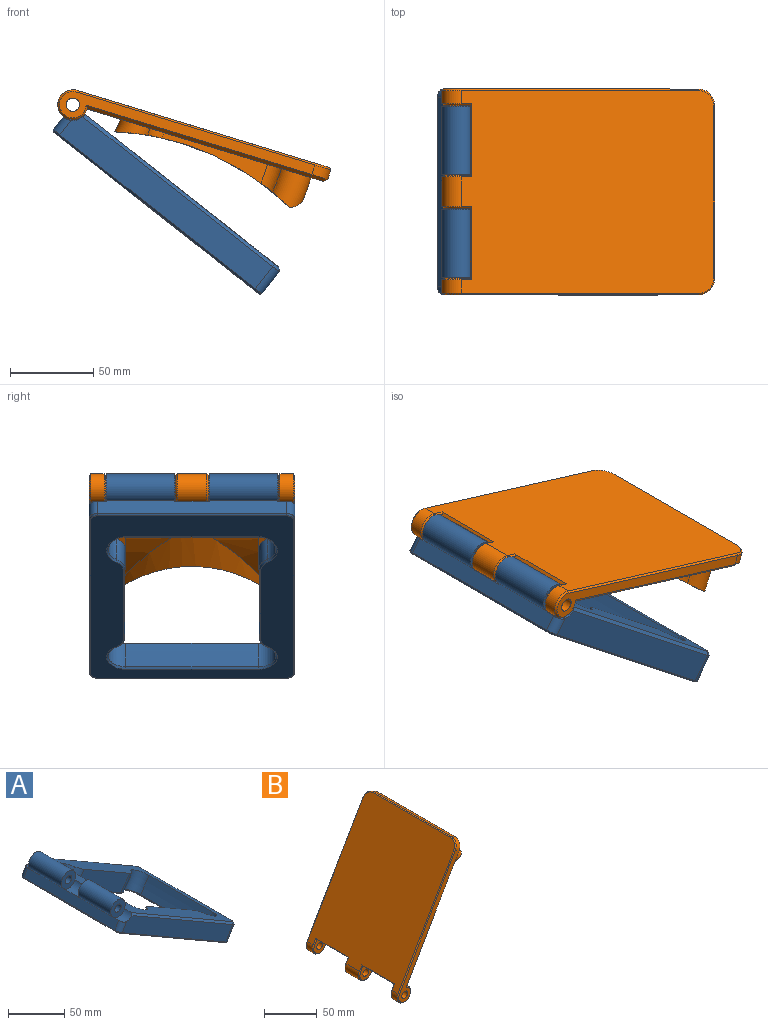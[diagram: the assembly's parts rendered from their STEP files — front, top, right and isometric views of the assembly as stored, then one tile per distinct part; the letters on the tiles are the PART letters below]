
ASSEMBLY  parts=2 mates=1
PART A: 58 faces, bbox 147.2x124.1x105.9 mm
  f0: plane 129.04x120mm, normal (0.5,0,0.87), area 7421.1mm2, adj f1,f3,f4,f6,f8,f9,f14,f15
  f1: plane 18.5x18mm, normal (0,-1,0), area 211.5mm2, adj f0,f2,f4,f5,f28
  f2: cylinder r=4mm len=41mm, axis (0,1,0), area 1030.4mm2, adj f1,f3
  f3: plane 18.5x18mm, normal (0,1,0), area 211.5mm2, adj f0,f2,f4,f5,f27
  f4: cylinder r=9mm len=41mm, axis (0,1,0), area 1738.9mm2, adj f0,f1,f3,f5
  f5: plane 114x8.66mm, normal (-0.87,0,0.5), area 1124mm2, adj f1,f3,f4,f6,f8,f9,f26,f27
  f6: plane 18.5x18mm, normal (0,-1,0), area 211.5mm2, adj f0,f5,f7,f9,f26
  f7: cylinder r=4mm len=41mm, axis (0,1,0), area 1030.4mm2, adj f6,f8
  f8: plane 18.5x18mm, normal (0,1,0), area 211.5mm2, adj f0,f5,f7,f9,f28
  f9: cylinder r=9mm len=41mm, axis (0,1,0), area 1738.9mm2, adj f0,f5,f6,f8
  f10: plane 138.4x87.58mm, normal (0,1,0), area 2533.2mm2, adj f27,f29,f32,f39,f53
  f11: plane 136.92x122.09mm, normal (-0.5,0,-0.87), area 7828.6mm2, adj f33,f34,f35,f36,f37,f38,f39,f40
  f12: plane 114x14.72mm, normal (0.87,0,-0.5), area 1938mm2, adj f29,f30,f35,f55
  f13: plane 138.4x87.58mm, normal (0,-1,0), area 2533.2mm2, adj f26,f30,f31,f34,f57
  f14: torus R=57.32mm, axis (0,1,0), area 192.7mm2, adj f0,f15,f25,f41
  f15: torus R=40mm, axis (0,1,0), area 561.5mm2, adj f0,f14,f16,f43
  f16: cylinder r=29.6mm len=80mm, axis (0,1,0), area 1720.6mm2, adj f0,f15,f17,f45
  f17: torus R=40mm, axis (0,1,0), area 561.5mm2, adj f0,f16,f18,f47
  f18: torus R=57.32mm, axis (0,1,0), area 192.8mm2, adj f0,f17,f19,f49
  f19: plane 68.91x48.4mm, normal (0,1,0), area 1252.8mm2, adj f0,f18,f20,f51
  f20: torus R=122.68mm, axis (0,1,0), area 193.1mm2, adj f0,f19,f21,f52
  f21: torus R=140mm, axis (0,1,0), area 525.4mm2, adj f0,f20,f22,f50
  f22: cylinder r=150.4mm len=80mm, axis (0,1,0), area 1514mm2, adj f0,f21,f23,f48
  f23: torus R=140mm, axis (0,1,0), area 525.4mm2, adj f0,f22,f24,f46
  f24: torus R=122.68mm, axis (0,1,0), area 193.1mm2, adj f0,f23,f25,f44
  f25: plane 68.92x48.4mm, normal (0,-1,0), area 1252.9mm2, adj f0,f14,f24,f42
  f26: cylinder r=9.5mm len=12.98mm, axis (0,1,0), area 149.2mm2, adj f0,f5,f6,f13,f31,f57
  f27: cylinder r=9.5mm len=12.98mm, axis (0,1,0), area 149.2mm2, adj f0,f3,f5,f10,f32,f53
  f28: cylinder r=9.5mm len=21mm, axis (0,1,0), area 313.4mm2, adj f0,f1,f5,f8
  f29: cylinder r=5mm len=17.22mm, axis (0.5,0,0.87), area 133.5mm2, adj f10,f12,f37,f54
  f30: cylinder r=5mm len=17.22mm, axis (-0.5,0,-0.87), area 133.5mm2, adj f12,f13,f33,f56
  f31: cylinder r=5mm len=11.96mm, axis (0.5,0,0.87), area 80.2mm2, adj f5,f13,f26,f36
  f32: cylinder r=5mm len=11.96mm, axis (-0.5,0,-0.87), area 80.2mm2, adj f5,f10,f27,f40
  f33: cone r=4mm half-angle=45deg, axis (0.5,0,0.87), area 10mm2, adj f11,f30,f34,f35
  f34: plane 130.4x75.87mm, normal (-0.35,-0.71,-0.61), area 212.1mm2, adj f11,f13,f33,f36
  f35: plane 114x1.37mm, normal (0.26,0,-0.97), area 161.2mm2, adj f11,f12,f33,f37
  f36: cone r=4mm half-angle=45deg, axis (0.5,0,0.87), area 10mm2, adj f11,f31,f34,f38
  f37: cone r=4mm half-angle=45deg, axis (0.5,0,0.87), area 10mm2, adj f11,f29,f35,f39
  f38: plane 114x1.37mm, normal (-0.97,0,-0.26), area 161.2mm2, adj f5,f11,f36,f40
  f39: plane 130.4x75.87mm, normal (-0.35,0.71,-0.61), area 212.1mm2, adj f10,f11,f37,f40
  f40: cone r=4mm half-angle=45deg, axis (0.5,0,0.87), area 10mm2, adj f11,f32,f38,f39
  f41: bspline ~7.43x5.54mm, area 15.2mm2, adj f11,f14,f42,f43
  f42: plane 58.63x34.43mm, normal (-0.35,-0.71,-0.61), area 94.5mm2, adj f11,f25,f41,f44
  f43: bspline ~21.44x12.38mm, area 39.9mm2, adj f11,f15,f41,f45
  f44: bspline ~7.7x5.33mm, area 13.1mm2, adj f11,f24,f42,f46
  f45: plane 80x0.82mm, normal (-0.1,0,-0.99), area 65.5mm2, adj f11,f16,f43,f47
  f46: bspline ~18.6x11.66mm, area 41mm2, adj f11,f23,f44,f48
  f47: bspline ~21.44x12.38mm, area 39.9mm2, adj f11,f17,f45,f49
  f48: plane 80x1.47mm, normal (-0.98,0,-0.2), area 120mm2, adj f11,f22,f46,f50
  f49: bspline ~7.43x5.54mm, area 15.2mm2, adj f11,f18,f47,f51
  f50: bspline ~18.6x11.65mm, area 41mm2, adj f11,f21,f48,f52
  f51: plane 58.63x34.43mm, normal (-0.35,0.71,-0.61), area 94.8mm2, adj f11,f19,f49,f52
  f52: bspline ~7.7x5.33mm, area 13.1mm2, adj f11,f20,f50,f51
  f53: plane 127.2x74.49mm, normal (0.35,0.71,0.61), area 411.7mm2, adj f0,f10,f27,f54
  f54: cone r=3mm half-angle=45deg, axis (-0.5,0,-0.87), area 17.8mm2, adj f0,f29,f53,f55
  f55: plane 114x2.73mm, normal (0.97,0,0.26), area 322.4mm2, adj f0,f12,f54,f56
  f56: cone r=3mm half-angle=45deg, axis (-0.5,0,-0.87), area 17.8mm2, adj f0,f30,f55,f57
  f57: plane 127.2x74.49mm, normal (0.35,-0.71,0.61), area 411.7mm2, adj f0,f13,f26,f56
PART B: 57 faces, bbox 102.5x124.1x151.6 mm
  f0: cylinder r=4mm len=20mm, axis (0,1,0), area 502.7mm2, adj f8,f9
  f1: cylinder r=4mm len=10mm, axis (0,1,0), area 251.3mm2, adj f11,f12
  f2: plane 129.9x120mm, normal (0.87,0,-0.5), area 7552mm2, adj f4,f6,f8,f9,f10,f11,f13,f18
  f3: plane 137.7x122mm, normal (-0.87,0,0.5), area 18764.8mm2, adj f6,f10,f13,f36,f37,f38,f41,f42
  f4: plane 17.57x16mm, normal (0,-1,0), area 166.7mm2, adj f2,f5,f34,f40,f41,f42
  f5: cylinder r=4mm len=10mm, axis (0,1,0), area 251.3mm2, adj f4,f7
  f6: cylinder r=9mm len=18mm, axis (0,1,0), area 339.8mm2, adj f2,f3,f40,f45,f56
  f7: plane 141.9x81.27mm, normal (0,1,0), area 1016.4mm2, adj f5,f15,f45,f46,f56
  f8: plane 17.57x16mm, normal (0,-1,0), area 166.7mm2, adj f0,f2,f33,f35,f36,f37
  f9: plane 17.57x16mm, normal (0,1,0), area 166.7mm2, adj f0,f2,f34,f42,f43,f44
  f10: cylinder r=9mm len=18mm, axis (0,1,0), area 763.4mm2, adj f2,f3,f35,f44
  f11: plane 17.57x16mm, normal (0,1,0), area 166.7mm2, adj f1,f2,f33,f37,f38,f39
  f12: plane 141.9x81.27mm, normal (0,-1,0), area 1016.4mm2, adj f1,f16,f50,f51,f52
  f13: cylinder r=9mm len=18mm, axis (0,1,0), area 339.8mm2, adj f2,f3,f39,f51,f52
  f14: plane 104x5.2mm, normal (0.5,0,0.87), area 624mm2, adj f15,f16,f48,f54
  f15: cylinder r=10mm len=11.66mm, axis (0.87,0,-0.5), area 94.2mm2, adj f7,f14,f47,f55
  f16: cylinder r=10mm len=11.66mm, axis (0.87,0,-0.5), area 94.2mm2, adj f12,f14,f49,f53
  f17: cylinder r=158.38mm len=92.47mm, axis (0,1,0), area 2497.1mm2, adj f18,f19,f20,f27,f28,f29,f31,f32
  f18: torus R=57.32mm, axis (0,1,0), area 41.4mm2, adj f2,f17,f19,f29
  f19: torus R=40mm, axis (0,1,0), area 169mm2, adj f2,f17,f18,f20
  f20: cylinder r=30mm len=80mm, axis (0,1,0), area 471mm2, adj f2,f17,f19,f21,f30,f31
  f21: torus R=40mm, axis (0,1,0), area 169mm2, adj f2,f20,f22,f30
  f22: torus R=57.32mm, axis (0,1,0), area 41.4mm2, adj f2,f21,f23,f30
  f23: plane 58.43x42.77mm, normal (0,-1,0), area 357mm2, adj f2,f22,f24,f30
  f24: torus R=122.68mm, axis (0,1,0), area 144mm2, adj f2,f23,f25,f30
  f25: torus R=140mm, axis (0,1,0), area 470.2mm2, adj f2,f24,f26,f30,f32
  f26: cylinder r=150mm len=80mm, axis (0,1,0), area 537.6mm2, adj f2,f25,f27,f32
  f27: torus R=140mm, axis (0,1,0), area 470.2mm2, adj f2,f17,f26,f28,f32
  f28: torus R=122.68mm, axis (0,1,0), area 144mm2, adj f2,f17,f27,f29
  f29: plane 58.43x42.77mm, normal (0,1,0), area 357mm2, adj f2,f17,f18,f28
  f30: cylinder r=158.38mm len=92.47mm, axis (0,1,0), area 2497.1mm2, adj f20,f21,f22,f23,f24,f25,f31,f32
  f31: cylinder r=75.17mm len=55.47mm, axis (0.5,0,0.87), area 1104mm2, adj f17,f20,f30
  f32: cylinder r=75.17mm len=97.83mm, axis (0.5,0,0.87), area 4486.4mm2, adj f17,f25,f26,f27,f30
  f33: cylinder r=9.5mm len=42mm, axis (0,1,0), area 345.6mm2, adj f2,f8,f11,f37
  f34: cylinder r=9.5mm len=42mm, axis (0,1,0), area 345.6mm2, adj f2,f4,f9,f42
  f35: cone r=9mm half-angle=45deg, axis (0,1,0), area 56.6mm2, adj f2,f8,f10,f36
  f36: plane 6.39x4.08mm, normal (-0.61,-0.71,0.35), area 9.4mm2, adj f3,f8,f35,f37
  f37: plane 44x1.44mm, normal (-0.77,0,-0.64), area 79.9mm2, adj f3,f8,f11,f33,f36,f38
  f38: plane 6.39x4.08mm, normal (-0.61,0.71,0.35), area 9.4mm2, adj f3,f11,f37,f39
  f39: cone r=8mm half-angle=45deg, axis (0,-1,0), area 56.6mm2, adj f2,f11,f13,f38
  f40: cone r=9mm half-angle=45deg, axis (0,1,0), area 56.6mm2, adj f2,f4,f6,f41
  f41: plane 6.39x4.08mm, normal (-0.61,-0.71,0.35), area 9.4mm2, adj f3,f4,f40,f42
  f42: plane 44x1.44mm, normal (-0.77,0,-0.64), area 79.9mm2, adj f3,f4,f9,f34,f41,f43
  f43: plane 6.39x4.08mm, normal (-0.61,0.71,0.35), area 9.4mm2, adj f3,f9,f42,f44
  f44: cone r=8mm half-angle=45deg, axis (0,-1,0), area 56.6mm2, adj f2,f9,f10,f43
  f45: cone r=8mm half-angle=45deg, axis (0,-1,0), area 58.8mm2, adj f6,f7,f46,f56
  f46: plane 130.4x75.87mm, normal (-0.61,0.71,0.35), area 212.1mm2, adj f3,f7,f45,f47
  f47: cone r=9mm half-angle=45deg, axis (0.87,0,-0.5), area 21.1mm2, adj f3,f15,f46,f48
  f48: plane 104x1.37mm, normal (-0.26,0,0.97), area 147.1mm2, adj f3,f14,f47,f49
  f49: cone r=9mm half-angle=45deg, axis (0.87,0,-0.5), area 21.1mm2, adj f3,f16,f48,f50
  f50: plane 130.4x75.87mm, normal (-0.61,-0.71,0.35), area 212.1mm2, adj f3,f12,f49,f51
  f51: cone r=9mm half-angle=45deg, axis (0,1,0), area 58.8mm2, adj f12,f13,f50,f52
  f52: plane 123.26x72.92mm, normal (0.61,-0.71,-0.35), area 399.7mm2, adj f2,f12,f13,f51,f53
  f53: cone r=10mm half-angle=45deg, axis (-0.87,0,0.5), area 40mm2, adj f2,f16,f52,f54
  f54: plane 104x2.73mm, normal (0.97,0,0.26), area 294.2mm2, adj f2,f14,f53,f55
  f55: cone r=10mm half-angle=45deg, axis (-0.87,0,0.5), area 40mm2, adj f2,f15,f54,f56
  f56: plane 123.26x72.92mm, normal (0.61,0.71,-0.35), area 399.7mm2, adj f2,f6,f7,f45,f55
PLACE A rot(axis=(0,1,0),8.2deg) t=(-67.58,27.36,170.81)mm
PLACE B rot(axis=(0,1,0),77deg) t=(-136.42,27.36,96.02)mm
MATE revolute B.f19 <-> A.f2  axis (0,-1,0) through (-156.65,17.36,183.72)mm
